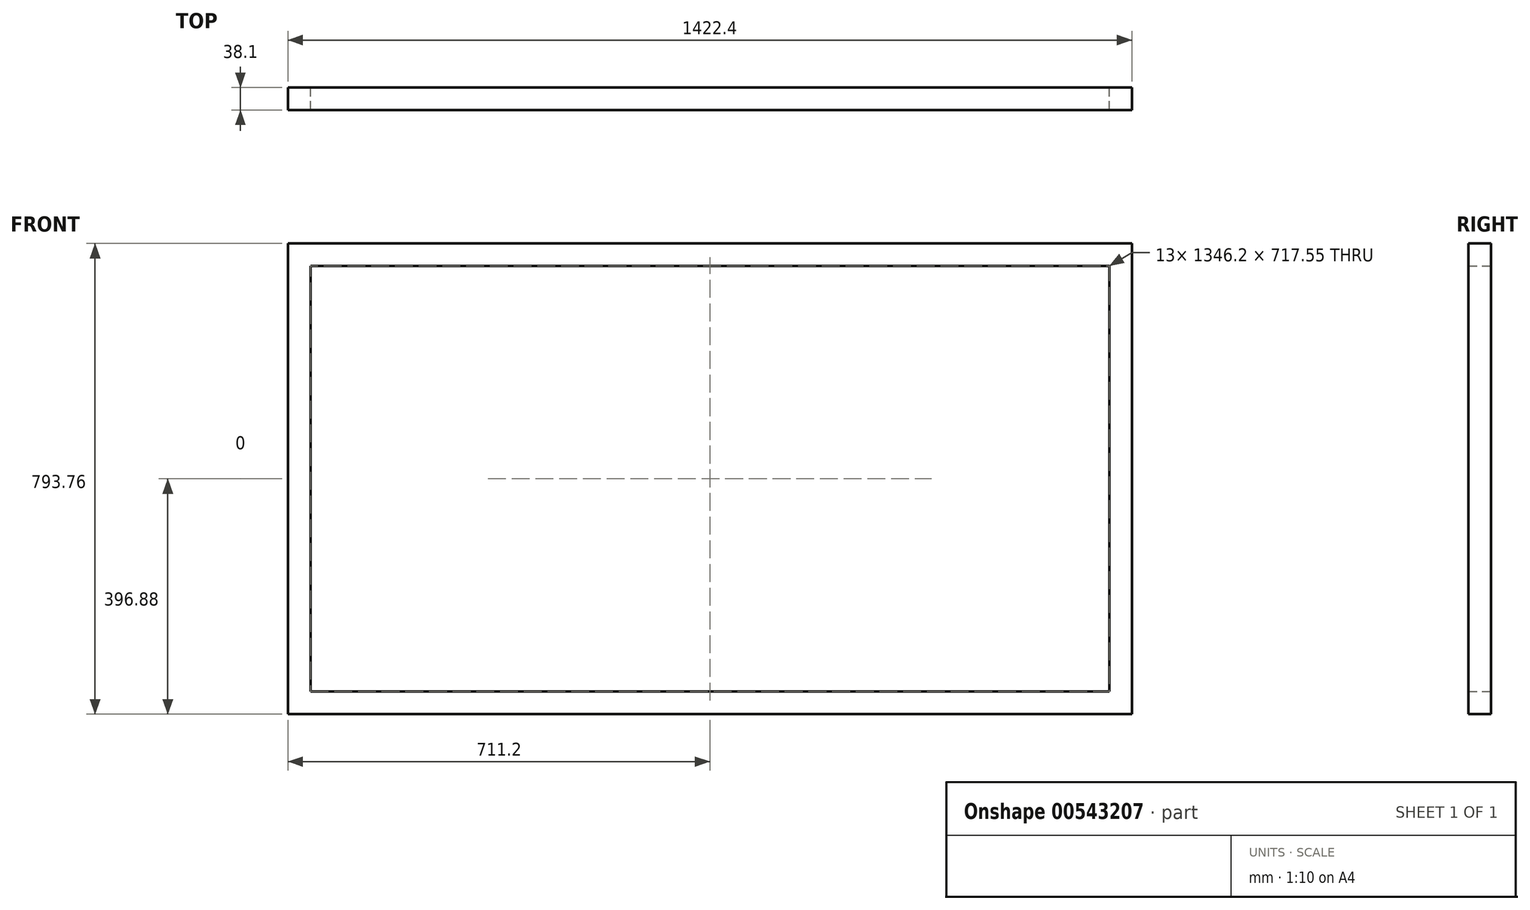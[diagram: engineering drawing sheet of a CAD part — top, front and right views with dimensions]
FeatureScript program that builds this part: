
annotation { "Feature Type Name" : "Feature", "Feature Type Description" : "" }
export const myFeature = defineFeature(function(context is Context, id is Id, definition is map)
    precondition{}
    {
        {
            var Q0;
            Q0=qCreatedBy(makeId("Front.planeOp"),FACE);
            var sketch = newSketch(context, id + "F0", { "sketchPlane" : qUnion([Q0])});
            skLineSegment(sketch, "E0.bottom", {"start": v(711.2, 396.88) * mm, "end": v(-711.2, 396.88) * mm});
            skLineSegment(sketch, "E0.top", {"start": v(711.2, -396.88) * mm, "end": v(-711.2, -396.88) * mm});
            skLineSegment(sketch, "E0.left", {"start": v(711.2, 396.88) * mm, "end": v(711.2, -396.88) * mm});
            skLineSegment(sketch, "E0.right", {"start": v(-711.2, 396.88) * mm, "end": v(-711.2, -396.88) * mm});
            skPoint(sketch, "E0.middle", {"position": v(0, 0) * mm});
            skLineSegment(sketch, "E1.bottom", {"start": v(673.1, 358.78) * mm, "end": v(-673.1, 358.78) * mm});
            skLineSegment(sketch, "E1.top", {"start": v(673.1, -358.77) * mm, "end": v(-673.1, -358.77) * mm});
            skLineSegment(sketch, "E1.left", {"start": v(673.1, 358.78) * mm, "end": v(673.1, -358.77) * mm});
            skLineSegment(sketch, "E1.right", {"start": v(-673.1, 358.78) * mm, "end": v(-673.1, -358.77) * mm});
            skLineSegment(sketch, "E2", {"start": v(-241.3, 396.88) * mm, "end": v(-241.3, -396.88) * mm});
            skLineSegment(sketch, "E3", {"start": v(0, 396.88) * mm, "end": v(0, -396.88) * mm});
            skLineSegment(sketch, "E4.MirrorCS", {"start": v(241.3, 396.88) * mm, "end": v(241.3, -396.88) * mm});
            skLineSegment(sketch, "E5", {"start": v(-711.2, 0) * mm, "end": v(711.2, 0) * mm});
            skSolve(sketch);
        }
        {
            var Q0;
            Q0 = qSketchRegion(id + "F0", true);
            extrude(context, id + "F1", {"entities" : qUnion([Q0]), "depth" : 38.1 * mm, "offsetDistance" : 25.4 * mm});
        }
    });
